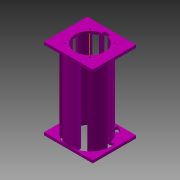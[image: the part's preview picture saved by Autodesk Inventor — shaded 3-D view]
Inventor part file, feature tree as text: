
AUTODESK INVENTOR PART (.ipt)
format: ipt  version: 2013 (Build 170138000, 138)  size: 227,840 bytes
history: native  units: mm
features: sketch x10, extrude x9, other x2, hole x1, pattern_circular x1
ambient origin geometry x8: Origin, YZ Plane, XZ Plane, XY Plane, X Axis, Y Axis, Z Axis, Center Point
feature tree (23):
  other  "ソリッド1"
  extrude  "押し出し1"  Depth=90.0mm
  extrude  "押し出し2"  Depth=80.0mm
  extrude  "押し出し3"  Depth=5.0mm TaperAngle=0.0deg
  extrude  "押し出し4"  Depth=80.0mm
  extrude  "押し出し5"  Depth=140.0mm TaperAngle=0.0deg
  extrude  "押し出し8"  Depth=55.0mm
  extrude  "押し出し9"  Depth=145.0mm TaperAngle=0.0deg
  hole  "穴2"  [1 undecoded]
  extrude  "押し出し12"  Depth=80.0mm
  other  "作業軸1"
  pattern_circular  "円形状パターン1"  [2 undecoded]
  extrude  "押し出し13"  Depth=11.0mm
  sketch  "スケッチ1"
  sketch  "スケッチ2"
  sketch  "スケッチ3"
  sketch  "スケッチ4"
  sketch  "スケッチ5"
  sketch  "スケッチ7"
  sketch  "スケッチ10"
  sketch  "スケッチ11"
  sketch  "スケッチ16"
  sketch  "スケッチ18"
note: 3 required parameter values undecoded (feature->parameter linkage not recoverable at this tier; creation-order binding heuristic only, values carry confidence <= 0.55)
